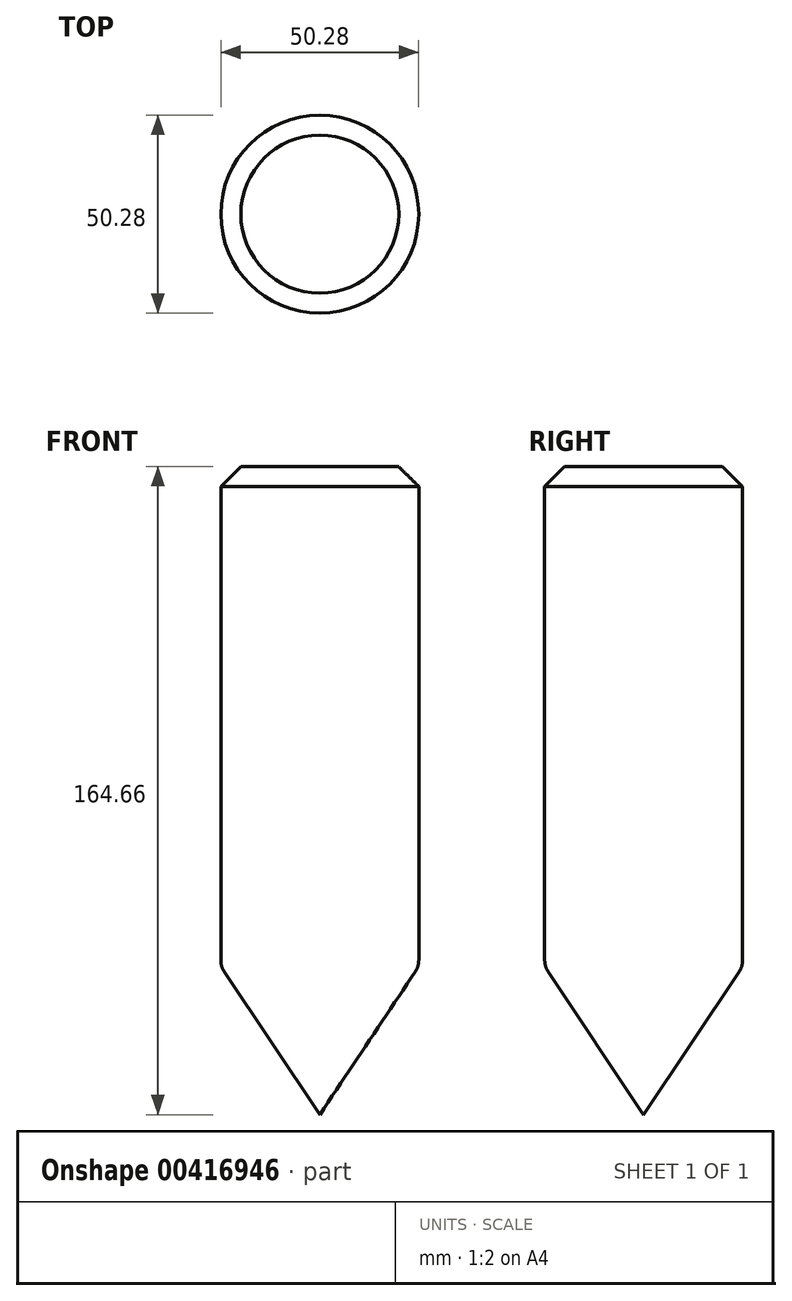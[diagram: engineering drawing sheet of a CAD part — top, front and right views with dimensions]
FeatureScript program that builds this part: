
annotation { "Feature Type Name" : "Feature", "Feature Type Description" : "" }
export const myFeature = defineFeature(function(context is Context, id is Id, definition is map)
    precondition{}
    {
        {
            var Q0;
            Q0=qCreatedBy(makeId("Top.planeOp"),FACE);
            var sketch = newSketch(context, id + "F0", { "sketchPlane" : qUnion([Q0])});
            skCircle(sketch, "E0", {"center": v(0, 0) * mm, "radius": 25.14 * mm});
            skSolve(sketch);
        }
        {
            var Q0;
            Q0=makeQuery(id+"F0.imprint","IMPRINT",FACE,{"disambiguationData":[TD([[makeQuery(id+"F0.imprint","IMPRINT",EDGE,{"derivedFrom":sQuery(id+"F0.wireOp",EDGE,"E0")}),1.0]])]});
            extrude(context, id + "F1", {"entities" : qUnion([Q0]), "depth" : 127 * mm, "offsetDistance" : 25.4 * mm});
        }
        {
            var Q0;
            Q0=qCreatedBy(makeId("Front.planeOp"),FACE);
            var sketch = newSketch(context, id + "F2", { "sketchPlane" : qUnion([Q0])});
            skPoint(sketch, "E1", {"position": v(0, -37.66) * mm});
            skSolve(sketch);
        }
        {
            var Q1;
            Q1=makeQuery(id+"F0.imprint","IMPRINT",FACE,{"disambiguationData":[TD([[makeQuery(id+"F0.imprint","IMPRINT",EDGE,{"derivedFrom":sQuery(id+"F0.wireOp",EDGE,"E0")}),1.0]])]});
            var Q2;
            Q2=sQuery(id+"F2.wireOp",VERTEX,"E1");
            loft(context, id + "F3", {"operationType" : NewBodyOperationType.ADD, "sheetProfilesArray" : [{ "sheetProfileEntities" : qUnion([Q1]) }, { "sheetProfileEntities" : qUnion([Q2]) }]});
        }
        {
            var Q0;
            {var subQ0=sQuery(id+"F0.wireOp",EDGE,"E0");Q0=makeQuery(id+"F3.boolean.opBoolean","MERGE",EDGE,{"derivedFrom":[makeQuery(id+"F1.opExtrude","CAP_EDGE",EDGE,{"disambiguationData":[OSD([subQ0])],"isStart":true}),makeQuery(id+"F3.opLoft","MID_CAP_EDGE",EDGE,{"disambiguationData":[OSD([subQ0,sQuery(id+"F2.wireOp",VERTEX,"E1")])],"capPos":0.0})]});}
            fillet(context, id + "F4", {"entities" : qUnion([Q0]), "radius" : 5.08 * mm, "tangentPropagation" : true, "allowEdgeOverflow" : false});
        }
        {
            var Q0;
            Q0=makeQuery(id+"F1.opExtrude","CAP_EDGE",EDGE,{"disambiguationData":[OSD([sQuery(id+"F0.wireOp",EDGE,"E0")])],"isStart":false});
            chamfer(context, id + "F5", {"entities" : qUnion([Q0]), "width" : 5.08 * mm, "tangentPropagation" : true});
        }
    });
